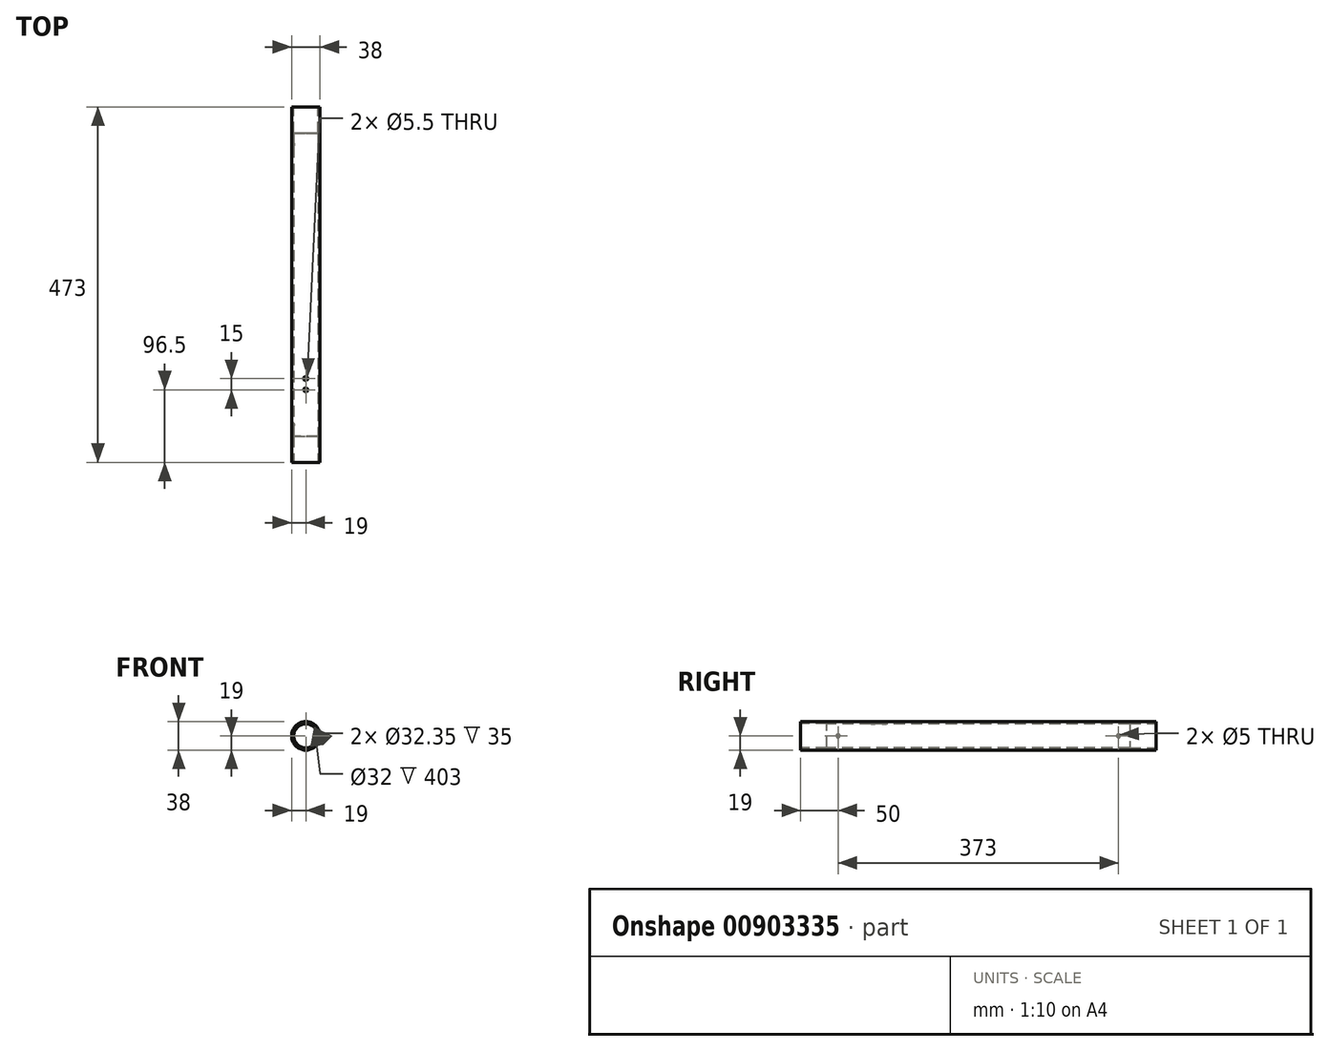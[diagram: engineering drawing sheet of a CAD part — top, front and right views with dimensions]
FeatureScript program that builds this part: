
annotation { "Feature Type Name" : "Feature", "Feature Type Description" : "" }
export const myFeature = defineFeature(function(context is Context, id is Id, definition is map)
    precondition{}
    {
        {
            var Q0;
            Q0=qCreatedBy(makeId("Front.planeOp"),FACE);
            var sketch = newSketch(context, id + "F0", { "sketchPlane" : qUnion([Q0])});
            skCircle(sketch, "E0", {"center": v(0, 0) * mm, "radius": 19 * mm});
            skSolve(sketch);
        }
        {
            var Q0;
            Q0 = qSketchRegion(id + "F0", true);
            extrude(context, id + "F1", {"entities" : qUnion([Q0]), "oppositeDirection" : true, "depth" : 473 * mm, "offsetDistance" : 25 * mm});
        }
        {
            var Q0;
            Q0=makeQuery(id+"F1.opExtrude","CAP_FACE",FACE,{"disambiguationData":[OSD([sQuery(id+"F0.wireOp",EDGE,"E0")])],"isStart":true});
            var sketch = newSketch(context, id + "F2", { "sketchPlane" : qUnion([Q0])});
            skCircle(sketch, "E1", {"center": v(0, 0) * mm, "radius": 16 * mm});
            skSolve(sketch);
        }
        {
            var Q0;
            Q0 = qSketchRegion(id + "F2", true);
            extrude(context, id + "F3", {"entities" : qUnion([Q0]), "operationType" : NewBodyOperationType.REMOVE, "endBound" : BoundingType.THROUGH_ALL, "oppositeDirection" : true, "depth" : 25 * mm, "offsetDistance" : 25 * mm});
        }
        {
            var Q0;
            Q0=makeQuery(id+"F1.opExtrude","CAP_FACE",FACE,{"disambiguationData":[OSD([sQuery(id+"F0.wireOp",EDGE,"E0")])],"isStart":true});
            var sketch = newSketch(context, id + "F4", { "sketchPlane" : qUnion([Q0])});
            skCircle(sketch, "E2", {"center": v(0, 0) * mm, "radius": 16.18 * mm});
            skSolve(sketch);
        }
        {
            var Q0;
            Q0 = qSketchRegion(id + "F4", true);
            extrude(context, id + "F5", {"entities" : qUnion([Q0]), "operationType" : NewBodyOperationType.REMOVE, "oppositeDirection" : true, "depth" : 35 * mm, "offsetDistance" : 25 * mm});
        }
        {
            var Q0;
            Q0=makeQuery(id+"F1.opExtrude","CAP_FACE",FACE,{"disambiguationData":[OSD([sQuery(id+"F0.wireOp",EDGE,"E0")])],"isStart":false});
            var sketch = newSketch(context, id + "F6", { "sketchPlane" : qUnion([Q0])});
            skCircle(sketch, "E3", {"center": v(0, 0) * mm, "radius": 16.18 * mm});
            skSolve(sketch);
        }
        {
            var Q0;
            Q0 = qSketchRegion(id + "F6", true);
            extrude(context, id + "F7", {"entities" : qUnion([Q0]), "operationType" : NewBodyOperationType.REMOVE, "oppositeDirection" : true, "depth" : 35 * mm, "offsetDistance" : 25 * mm});
        }
        {
            var Q0;
            Q0=qCreatedBy(makeId("Top.planeOp"),FACE);
            cPlane(context, id + "F8", {"entities" : qUnion([Q0]), "cplaneType" : CPlaneType.OFFSET, "offset" : 25 * mm, "width" : 150 * mm, "height" : 150 * mm});
        }
        {
            var Q0;
            Q0=qCreatedBy(id+"F8.planeOp",FACE);
            var sketch = newSketch(context, id + "F9", { "sketchPlane" : qUnion([Q0])});
            skPoint(sketch, "E4", {"position": v(0, 96.5) * mm});
            skPoint(sketch, "E5", {"position": v(0, 111.5) * mm});
            skSolve(sketch);
        }
        {
            var Q0;
            Q0=sQuery(id+"F9.wireOp",VERTEX,"E4");
            var Q1;
            Q1=sQuery(id+"F9.wireOp",VERTEX,"E5");
            var Q2;
            Q2=makeQuery(id+"F1.opExtrude","SWEPT_BODY",BODY,{"disambiguationData":[OSD([sQuery(id+"F0.wireOp",EDGE,"E0")])]});
            hole(context, id + "F10", {"style" : HoleStyle.SIMPLE, "endStyle" : HoleEndStyle.BLIND, "holeDiameter" : 5.5 * mm, "majorDiameter" : 5 * mm, "holeDepth" : 20 * mm, "tappedDepth" : 12 * mm, "tapClearance" : 3, "startFromSketch" : true, "locations" : qUnion([Q0, Q1]), "scope" : qUnion([Q2])});
        }
        {
            var Q0;
            Q0=qCreatedBy(makeId("Right.planeOp"),FACE);
            cPlane(context, id + "F11", {"entities" : qUnion([Q0]), "cplaneType" : CPlaneType.OFFSET, "offset" : 25 * mm, "oppositeDirection" : true, "width" : 150 * mm, "height" : 150 * mm});
        }
        {
            var Q0;
            Q0=qCreatedBy(id+"F11.planeOp",FACE);
            var sketch = newSketch(context, id + "F12", { "sketchPlane" : qUnion([Q0])});
            skPoint(sketch, "E6", {"position": v(50, 0) * mm});
            skPoint(sketch, "E7", {"position": v(423, 0) * mm});
            skSolve(sketch);
        }
        {
            var Q0;
            Q0=sQuery(id+"F12.wireOp",VERTEX,"E6");
            var Q1;
            Q1=sQuery(id+"F12.wireOp",VERTEX,"E7");
            var Q2;
            Q2=makeQuery(id+"F1.opExtrude","SWEPT_BODY",BODY,{"disambiguationData":[OSD([sQuery(id+"F0.wireOp",EDGE,"E0")])]});
            hole(context, id + "F13", {"style" : HoleStyle.SIMPLE, "endStyle" : HoleEndStyle.BLIND, "oppositeDirection" : true, "standardTappedOrClearance" : lookupTablePath({ "standard" : "ISO", "engagement" : "75%", "pitch" : "1 mm", "size" : "M6", "type" : "Tapped" }), "standardBlindInLast" : lookupTablePath({ "standard" : "ISO", "engagement" : "75%", "pitch" : "1 mm", "size" : "M6", "type" : "Tapped" }), "holeDiameter" : 5 * mm, "majorDiameter" : 6 * mm, "showTappedDepth" : true, "holeDepth" : 15 * mm, "tappedDepth" : 12 * mm, "tapClearance" : 3, "startFromSketch" : true, "locations" : qUnion([Q0, Q1]), "scope" : qUnion([Q2])});
        }
    });
